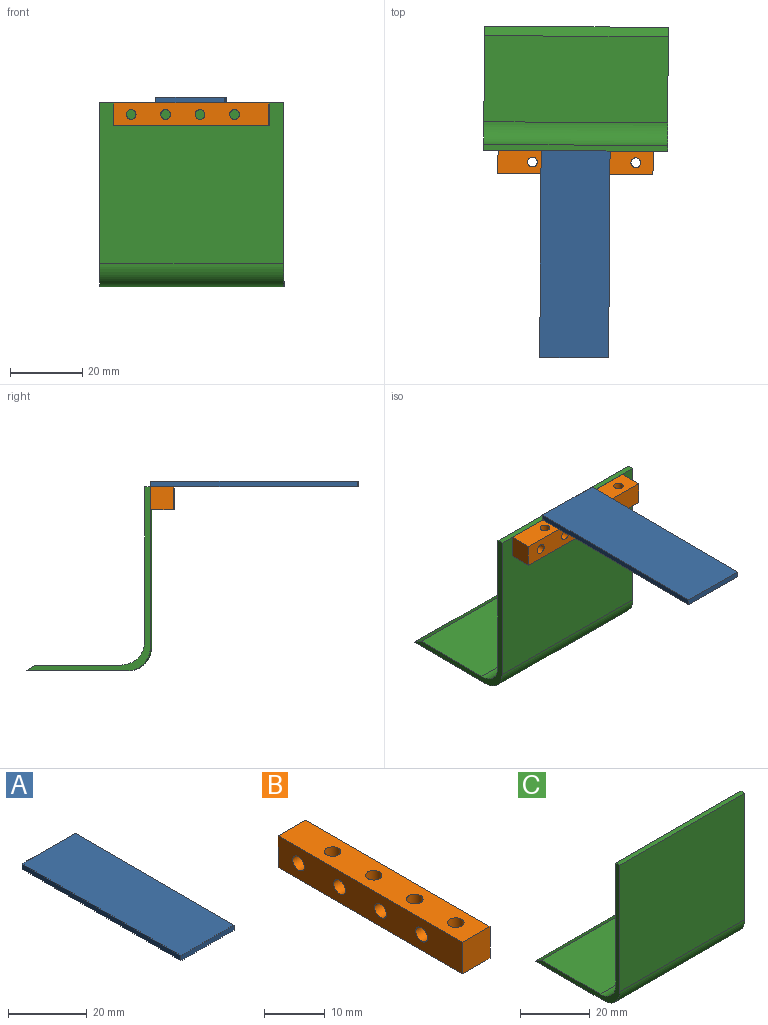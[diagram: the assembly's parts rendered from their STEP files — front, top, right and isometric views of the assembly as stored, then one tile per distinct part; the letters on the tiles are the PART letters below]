
ASSEMBLY  parts=3 mates=2
PART A: 6 faces, bbox 19.1x57.2x1.6 mm
  f0: plane 57.15x1.6mm, normal (-1,0,0), area 91.5mm2, adj f1,f3,f4,f5
  f1: plane 19.05x1.6mm, normal (0,-1,0), area 30.5mm2, adj f0,f2,f4,f5
  f2: plane 57.15x1.6mm, normal (1,0,0), area 91.5mm2, adj f1,f3,f4,f5
  f3: plane 19.05x1.6mm, normal (0,1,0), area 30.5mm2, adj f0,f2,f4,f5
  f4: plane 57.15x19.05mm, normal (0,0,1), area 1088.7mm2, adj f0,f1,f2,f3
  f5: plane 57.15x19.05mm, normal (0,0,-1), area 1088.7mm2, adj f0,f1,f2,f3
PART B: 14 faces, bbox 6.4x42.9x6.4 mm
  f0: revolved ~6.35x2.71mm, area 54mm2, adj f5,f7
  f1: revolved ~6.35x2.71mm, area 54mm2, adj f5,f7
  f2: revolved ~6.35x2.71mm, area 54mm2, adj f5,f7
  f3: revolved ~6.35x2.71mm, area 54mm2, adj f5,f7
  f4: plane 6.35x6.35mm, normal (0,-1,0), area 40.3mm2, adj f5,f7,f11,f12
  f5: plane 42.86x6.35mm, normal (0,0,-1), area 249.2mm2, adj f0,f1,f2,f3,f4,f6,f11,f12
  f6: plane 6.35x6.35mm, normal (0,1,0), area 40.3mm2, adj f5,f7,f11,f12
  f7: plane 42.86x6.35mm, normal (0,0,1), area 249.2mm2, adj f0,f1,f2,f3,f4,f6,f11,f12
  f8: revolved ~6.35x2.71mm, area 54mm2, adj f11,f12
  f9: revolved ~6.35x2.71mm, area 54mm2, adj f11,f12
  f10: revolved ~6.35x2.71mm, area 54mm2, adj f11,f12
  f11: plane 42.86x6.35mm, normal (-1,0,0), area 249.2mm2, adj f4,f5,f6,f7,f8,f9,f10,f13
  f12: plane 42.86x6.35mm, normal (1,0,0), area 249.2mm2, adj f4,f5,f6,f7,f8,f9,f10,f13
  f13: revolved ~6.35x2.71mm, area 54mm2, adj f11,f12
PART C: 10 faces, bbox 50.8x34.4x50.8 mm
  f0: plane 50.8x2.61mm, normal (0,0.52,0.85), area 155.7mm2, adj f1,f7,f8,f9
  f1: plane 50.8x23.8mm, normal (0,0,1), area 1209mm2, adj f0,f2,f8,f9
  f2: cylinder r=6.35mm len=50.8mm, axis (-1,0,0), area 506.7mm2, adj f1,f3,f8,f9
  f3: plane 50.8x42.85mm, normal (0,1,0), area 2176.8mm2, adj f2,f4,f8,f9
  f4: plane 50.8x1.6mm, normal (0,0,1), area 81.3mm2, adj f3,f5,f8,f9
  f5: plane 50.8x44.45mm, normal (0,-1,0), area 2258.1mm2, adj f4,f6,f8,f9
  f6: cylinder r=6.35mm len=50.8mm, axis (-1,0,0), area 506.7mm2, adj f5,f7,f8,f9
  f7: plane 50.8x28.01mm, normal (0,0,-1), area 1423.1mm2, adj f0,f6,f8,f9
  f8: plane 50.8x34.36mm, normal (1,0,0), area 131.6mm2, adj f0,f1,f2,f3,f4,f5,f6,f7
  f9: plane 50.8x34.36mm, normal (-1,0,0), area 131.6mm2, adj f0,f1,f2,f3,f4,f5,f6,f7
PLACE A rot(axis=(0,0,-1),0.4deg) t=(-3.16,-20.66,6.87)mm
PLACE B rot(axis=(0,0,1),89.6deg) t=(-54.4,-21.15,3.69)mm
PLACE C rot(axis=(0,0,-1),0.4deg) t=(-100.77,47.9,-50.16)mm
MATE fastened C.f5 <-> B.f12  axis (-0.01,-1,0) through (-75.81,-17.83,6.87)mm
MATE fastened A.f5 <-> B.f7  axis (0,0,-1) through (-75.81,-17.83,6.87)mm
